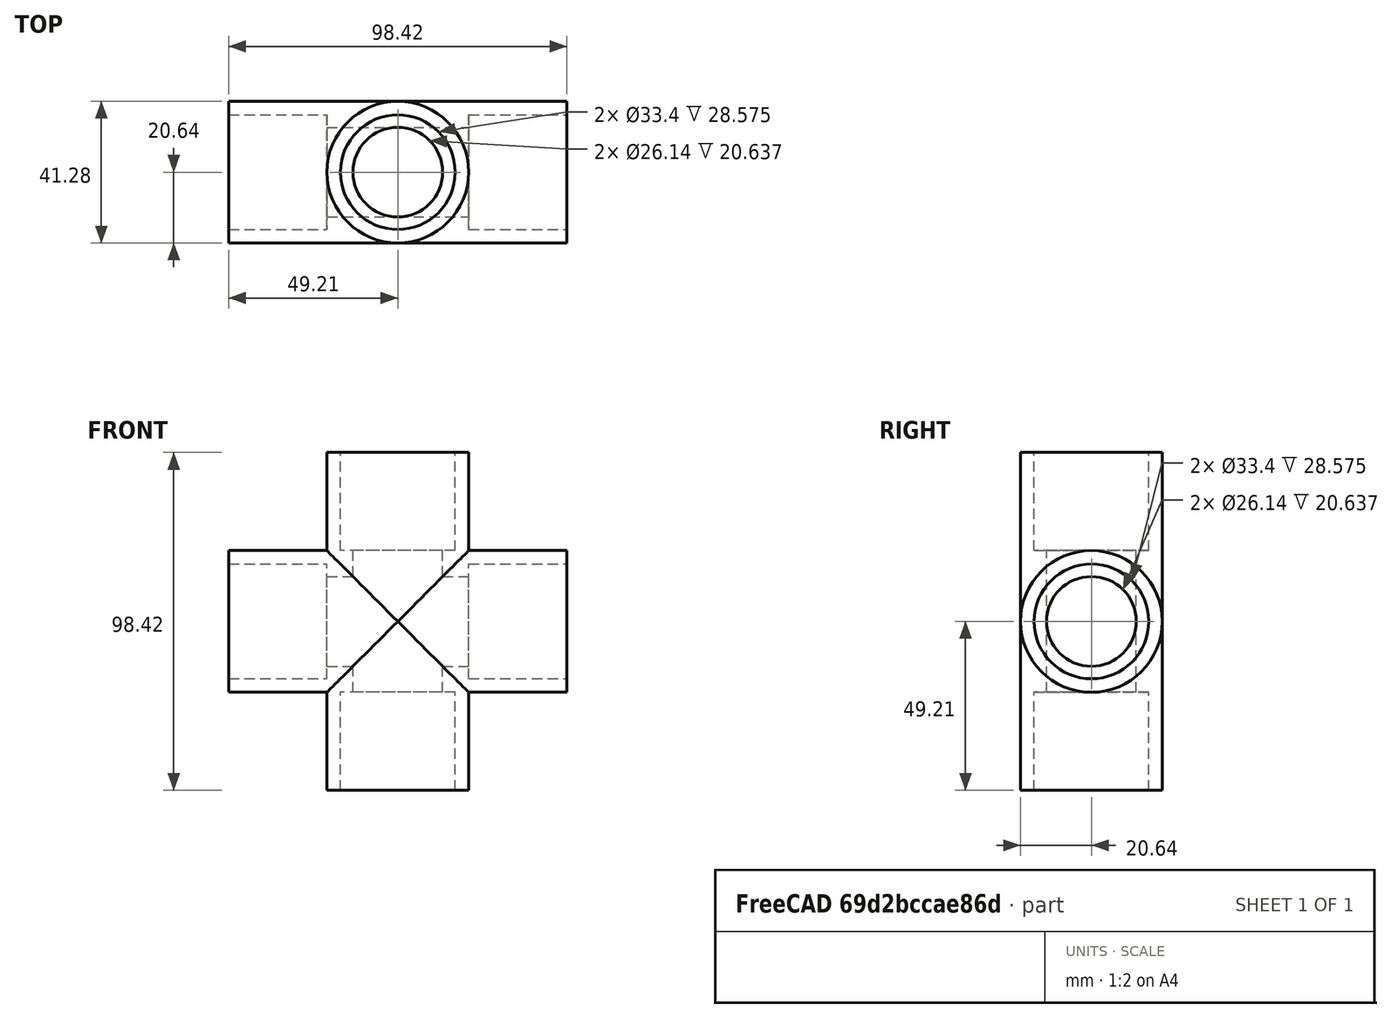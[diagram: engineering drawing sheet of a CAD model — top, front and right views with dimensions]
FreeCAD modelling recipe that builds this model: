
FCSTD DOCUMENT  (FreeCAD 0.17R13303 (Git))
Label: cross-test
License: All rights reserved
LicenseURL: http://en.wikipedia.org/wiki/All_rights_reserved
objects: Part::Cylinder×8, Part::MultiFuse×3, Part::Cut×2
note: 13 computed .brp shape members not serialized (recipe doc carries the construction recipe); baked Part::Feature solids carry a one-line shape summary decoded from their .brp

FEATURE [Part::Cylinder] VerticalOuterCynlider
  Angle = 360
  AttacherType = Attacher::AttachEngine3D
  Height = 98.425
  Placement = pos=(0,0,-49.2125) rot=(0,0,1;0rad)
  Radius = 20.6375
FEATURE [Part::Cylinder] VerticalInnerCynlider
  Angle = 360
  AttacherType = Attacher::AttachEngine3D
  Height = 108.267
  Placement = pos=(0,0,-54.1337) rot=(0,0,1;0rad)
  Radius = 13.0683
FEATURE [Part::Cylinder] HorizontalOuterCynlider
  Angle = 360
  AttacherType = Attacher::AttachEngine3D
  Height = 98.425
  Placement = pos=(-49.2125,0,0) rot=(0,1,0;1.5708rad)
  Radius = 20.6375
FEATURE [Part::Cylinder] HorizontalInnerCynlider
  Angle = 360
  AttacherType = Attacher::AttachEngine3D
  Height = 108.267
  Placement = pos=(-54.1337,0,0) rot=(0,1,0;1.5708rad)
  Radius = 13.0683
FEATURE [Part::MultiFuse] OuterCrossFusion
  Shapes = -> [VerticalOuterCynlider,HorizontalOuterCynlider]
FEATURE [Part::MultiFuse] InnerCrossFusion
  Shapes = -> [VerticalInnerCynlider,HorizontalInnerCynlider]
FEATURE [Part::Cut] Cut
  Base = -> OuterCrossFusion
  Tool = -> InnerCrossFusion
FEATURE [Part::Cylinder] SocketLeft
  Angle = 360
  AttacherType = Attacher::AttachEngine3D
  Height = 31.4325
  Placement = pos=(-52.07,0,0) rot=(0,1,0;1.5708rad)
  Radius = 16.7005
FEATURE [Part::Cylinder] SocketRight
  Angle = 360
  AttacherType = Attacher::AttachEngine3D
  Height = 31.4325
  Placement = pos=(20.6375,0,0) rot=(0,1,0;1.5708rad)
  Radius = 16.7005
FEATURE [Part::Cylinder] SocketTop
  Angle = 360
  AttacherType = Attacher::AttachEngine3D
  Height = 31.4325
  Placement = pos=(0,0,20.6375) rot=(0,0,1;0rad)
  Radius = 16.7005
FEATURE [Part::Cylinder] SocketBottom
  Angle = 360
  AttacherType = Attacher::AttachEngine3D
  Height = 31.4325
  Placement = pos=(0,0,-52.07) rot=(0,0,1;0rad)
  Radius = 16.7005
FEATURE [Part::MultiFuse] Sockets
  Shapes = -> [SocketLeft,SocketRight,SocketTop,SocketBottom]
FEATURE [Part::Cut] Cross  label="420-010"
  Base = -> Cut
  Tool = -> Sockets
